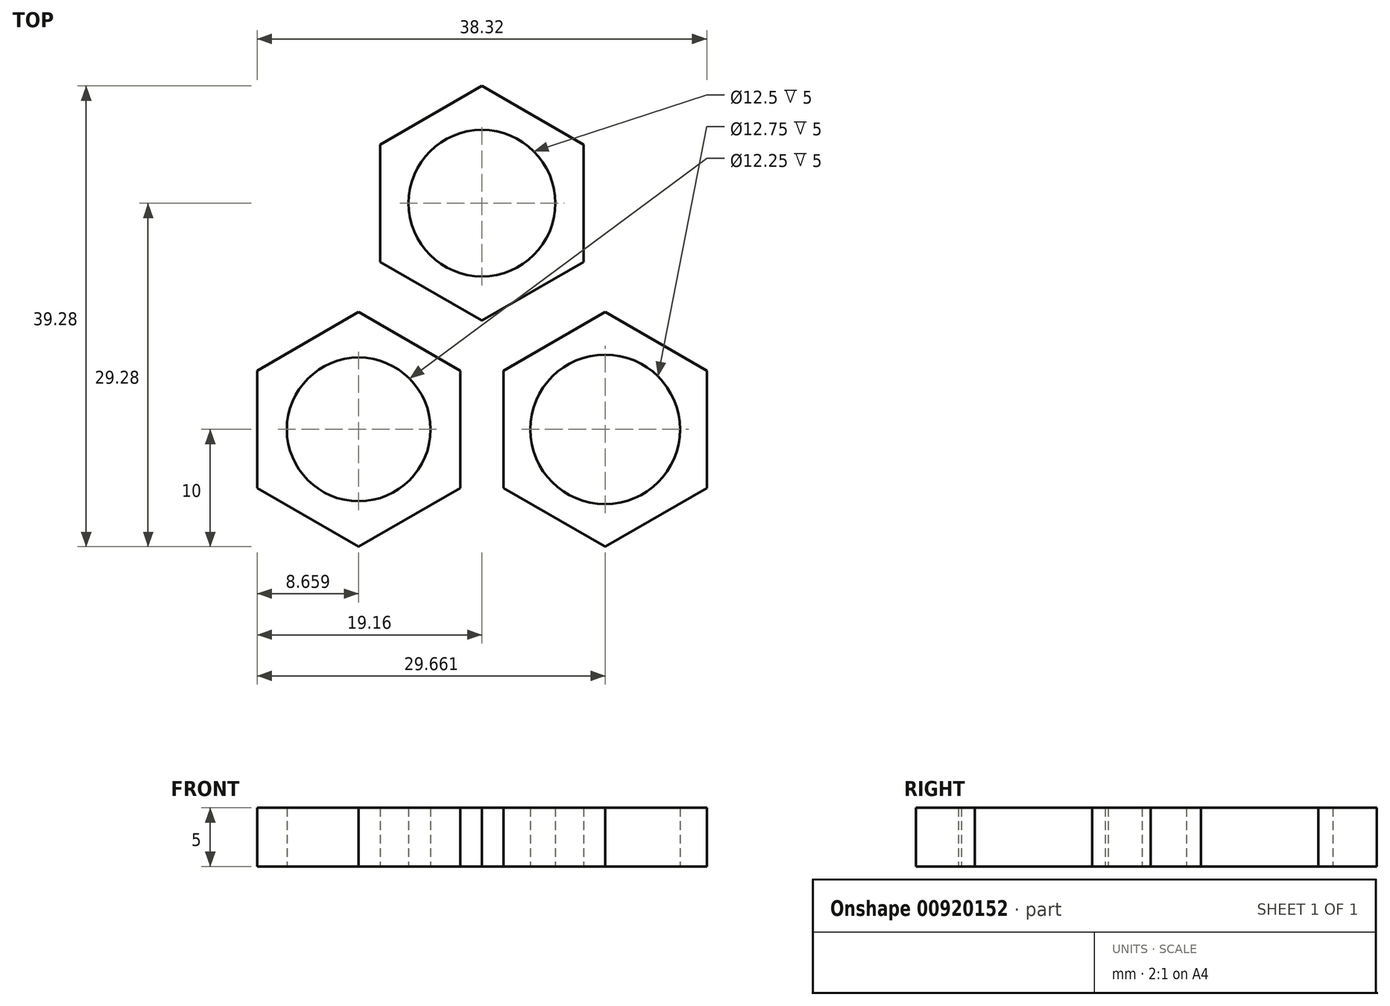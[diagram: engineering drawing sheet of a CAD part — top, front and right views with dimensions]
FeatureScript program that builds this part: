
annotation { "Feature Type Name" : "Feature", "Feature Type Description" : "" }
export const myFeature = defineFeature(function(context is Context, id is Id, definition is map)
    precondition{}
    {
        {
            var Q0;
            Q0=qCreatedBy(makeId("Top.planeOp"),FACE);
            var sketch = newSketch(context, id + "F0", { "sketchPlane" : qUnion([Q0])});
            skCircle(sketch, "E0", {"center": v(0, 0) * mm, "radius": 12.5 * mm, "construction": true});
            skCircle(sketch, "E1.cCircle", {"center": v(0, 12.5) * mm, "radius": 10 * mm, "construction": true});
            skLineSegment(sketch, "E1.0", {"start": v(0, 2.5) * mm, "end": v(-8.66, 7.5) * mm});
            skLineSegment(sketch, "E1.1", {"start": v(-8.66, 7.5) * mm, "end": v(-8.66, 17.5) * mm});
            skLineSegment(sketch, "E1.2", {"start": v(-8.66, 17.5) * mm, "end": v(0, 22.5) * mm});
            skLineSegment(sketch, "E1.3", {"start": v(0, 22.5) * mm, "end": v(8.66, 17.5) * mm});
            skLineSegment(sketch, "E1.4", {"start": v(8.66, 17.5) * mm, "end": v(8.66, 7.5) * mm});
            skLineSegment(sketch, "E1.5", {"start": v(8.66, 7.5) * mm, "end": v(0, 2.5) * mm});
            skCircle(sketch, "E2.cCircle", {"center": v(10.5, -6.78) * mm, "radius": 10 * mm, "construction": true});
            skLineSegment(sketch, "E2.0", {"start": v(19.16, -11.78) * mm, "end": v(10.5, -16.78) * mm});
            skLineSegment(sketch, "E2.1", {"start": v(10.5, -16.78) * mm, "end": v(1.84, -11.78) * mm});
            skLineSegment(sketch, "E2.2", {"start": v(1.84, -11.78) * mm, "end": v(1.84, -1.78) * mm});
            skLineSegment(sketch, "E2.3", {"start": v(1.84, -1.78) * mm, "end": v(10.5, 3.22) * mm});
            skLineSegment(sketch, "E2.4", {"start": v(10.5, 3.22) * mm, "end": v(19.16, -1.78) * mm});
            skLineSegment(sketch, "E2.5", {"start": v(19.16, -1.78) * mm, "end": v(19.16, -11.78) * mm});
            skCircle(sketch, "E3.cCircle", {"center": v(-10.5, -6.78) * mm, "radius": 10 * mm, "construction": true});
            skLineSegment(sketch, "E3.0", {"start": v(-1.84, -11.78) * mm, "end": v(-10.5, -16.78) * mm});
            skLineSegment(sketch, "E3.1", {"start": v(-10.5, -16.78) * mm, "end": v(-19.16, -11.78) * mm});
            skLineSegment(sketch, "E3.2", {"start": v(-19.16, -11.78) * mm, "end": v(-19.16, -1.78) * mm});
            skLineSegment(sketch, "E3.3", {"start": v(-19.16, -1.78) * mm, "end": v(-10.5, 3.22) * mm});
            skLineSegment(sketch, "E3.4", {"start": v(-10.5, 3.22) * mm, "end": v(-1.84, -1.78) * mm});
            skLineSegment(sketch, "E3.5", {"start": v(-1.84, -1.78) * mm, "end": v(-1.84, -11.78) * mm});
            skLineSegment(sketch, "E4", {"start": v(0, 0) * mm, "end": v(0, 2.5) * mm, "construction": true});
            skLineSegment(sketch, "E5", {"start": v(0, 0) * mm, "end": v(1.84, -1.78) * mm, "construction": true});
            skLineSegment(sketch, "E6", {"start": v(0, 0) * mm, "end": v(-1.84, -1.78) * mm, "construction": true});
            skCircle(sketch, "E7", {"center": v(-10.5, -6.78) * mm, "radius": 6.12 * mm});
            skCircle(sketch, "E8", {"center": v(0, 12.5) * mm, "radius": 6.25 * mm});
            skCircle(sketch, "E9", {"center": v(10.5, -6.78) * mm, "radius": 6.38 * mm});
            skSolve(sketch);
        }
        {
            var Q0;
            Q0=makeQuery(id+"F0.imprint","IMPRINT",FACE,{"disambiguationData":[TD([[makeQuery(id+"F0.imprint","IMPRINT",EDGE,{"derivedFrom":sQuery(id+"F0.wireOp",EDGE,"E1.0")}),-1.0]])]});
            var Q1;
            Q1=makeQuery(id+"F0.imprint","IMPRINT",FACE,{"disambiguationData":[TD([[makeQuery(id+"F0.imprint","IMPRINT",EDGE,{"derivedFrom":sQuery(id+"F0.wireOp",EDGE,"E3.0")}),-1.0]])]});
            var Q2;
            Q2=makeQuery(id+"F0.imprint","IMPRINT",FACE,{"disambiguationData":[TD([[makeQuery(id+"F0.imprint","IMPRINT",EDGE,{"derivedFrom":sQuery(id+"F0.wireOp",EDGE,"E2.0")}),-1.0]])]});
            extrude(context, id + "F1", {"entities" : qUnion([Q0, Q1, Q2]), "depth" : 5 * mm, "offsetDistance" : 25 * mm});
        }
    });
